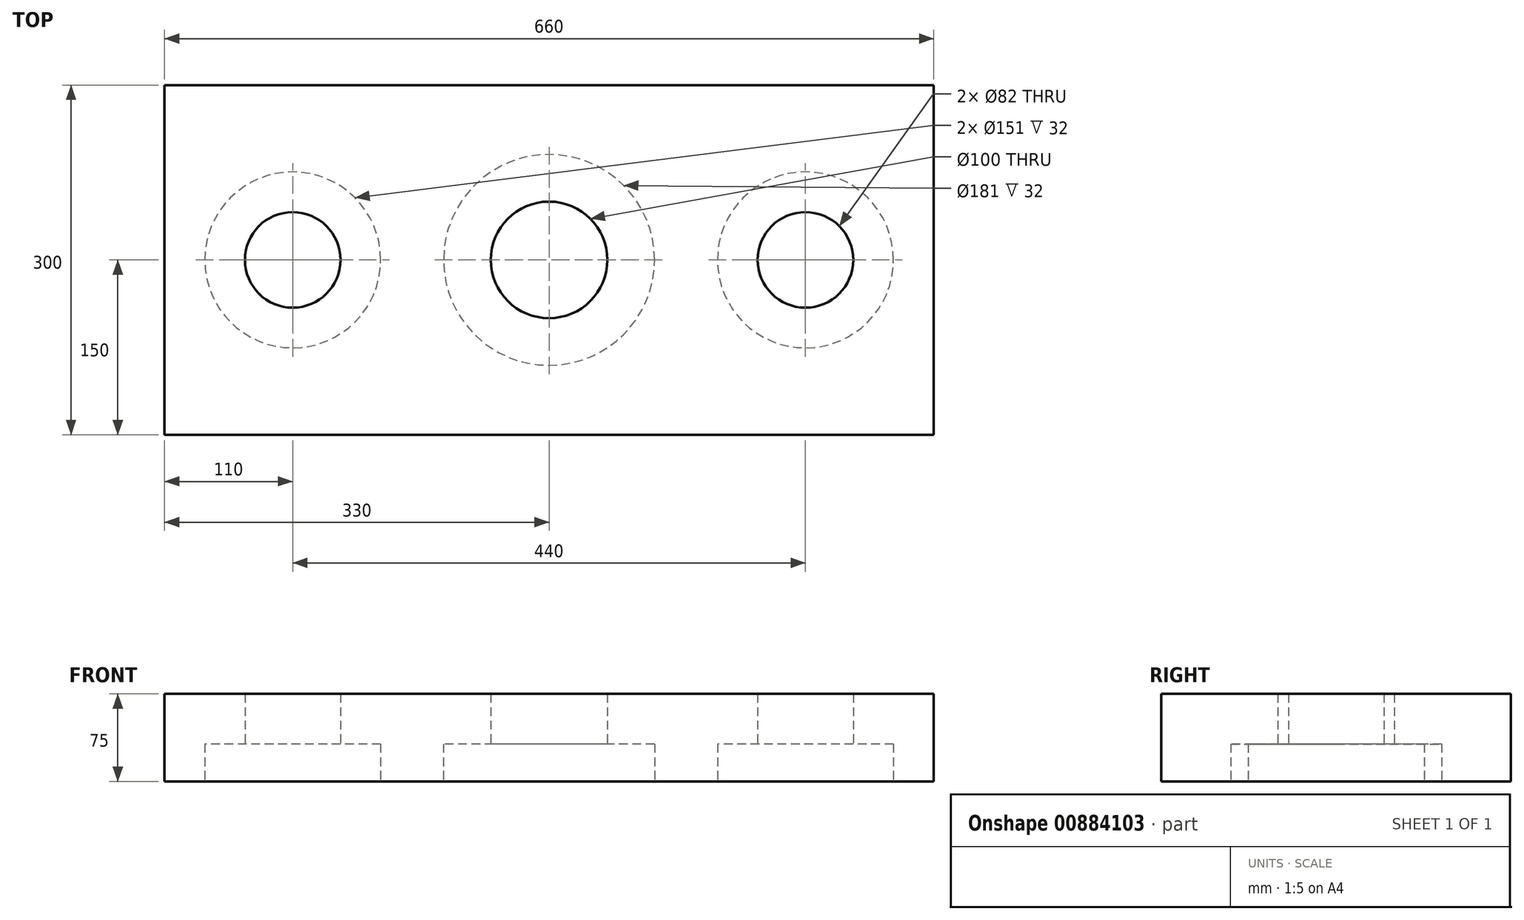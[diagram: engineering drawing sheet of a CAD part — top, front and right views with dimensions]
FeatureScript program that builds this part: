
annotation { "Feature Type Name" : "Feature", "Feature Type Description" : "" }
export const myFeature = defineFeature(function(context is Context, id is Id, definition is map)
    precondition{}
    {
        {
            var Q0;
            Q0=qCreatedBy(makeId("Top.planeOp"),FACE);
            var sketch = newSketch(context, id + "F0", { "sketchPlane" : qUnion([Q0])});
            skLineSegment(sketch, "E0.bottom", {"start": v(-330, 150) * mm, "end": v(330, 150) * mm});
            skLineSegment(sketch, "E0.top", {"start": v(-330, -150) * mm, "end": v(330, -150) * mm});
            skLineSegment(sketch, "E0.left", {"start": v(-330, 150) * mm, "end": v(-330, -150) * mm});
            skLineSegment(sketch, "E0.right", {"start": v(330, 150) * mm, "end": v(330, -150) * mm});
            skPoint(sketch, "E0.middle", {"position": v(0, 0) * mm});
            skLineSegment(sketch, "E1", {"start": v(-330, 0) * mm, "end": v(330, 0) * mm, "construction": true});
            skCircle(sketch, "E2", {"center": v(0, 0) * mm, "radius": 50 * mm});
            skCircle(sketch, "E3", {"center": v(0, 0) * mm, "radius": 90.5 * mm});
            skCircle(sketch, "E4", {"center": v(-220, 0) * mm, "radius": 41 * mm});
            skCircle(sketch, "E5", {"center": v(-220, 0) * mm, "radius": 75.5 * mm});
            skCircle(sketch, "E6", {"center": v(220, 0) * mm, "radius": 41 * mm});
            skCircle(sketch, "E7", {"center": v(220, 0) * mm, "radius": 75.5 * mm});
            skSolve(sketch);
        }
        {
            var Q0;
            Q0=makeQuery(id+"F0.imprint","IMPRINT",FACE,{"disambiguationData":[TD([[makeQuery(id+"F0.imprint","IMPRINT",EDGE,{"derivedFrom":sQuery(id+"F0.wireOp",EDGE,"E0.bottom")}),-1.0]])]});
            var Q1;
            Q1=makeQuery(id+"F0.imprint","IMPRINT",FACE,{"disambiguationData":[TD([[makeQuery(id+"F0.imprint","IMPRINT",EDGE,{"derivedFrom":sQuery(id+"F0.wireOp",EDGE,"E4")}),-1.0]])]});
            var Q2;
            Q2=makeQuery(id+"F0.imprint","IMPRINT",FACE,{"disambiguationData":[TD([[makeQuery(id+"F0.imprint","IMPRINT",EDGE,{"derivedFrom":sQuery(id+"F0.wireOp",EDGE,"E2")}),-1.0]])]});
            var Q3;
            Q3=makeQuery(id+"F0.imprint","IMPRINT",FACE,{"disambiguationData":[TD([[makeQuery(id+"F0.imprint","IMPRINT",EDGE,{"derivedFrom":sQuery(id+"F0.wireOp",EDGE,"E6")}),-1.0]])]});
            extrude(context, id + "F1", {"entities" : qUnion([Q0, Q1, Q2, Q3]), "depth" : 75 * mm, "offsetDistance" : 25 * mm});
        }
        {
            var Q0;
            Q0=makeQuery(id+"F0.imprint","IMPRINT",FACE,{"disambiguationData":[TD([[makeQuery(id+"F0.imprint","IMPRINT",EDGE,{"derivedFrom":sQuery(id+"F0.wireOp",EDGE,"E4")}),-1.0]])]});
            var Q1;
            Q1=makeQuery(id+"F0.imprint","IMPRINT",FACE,{"disambiguationData":[TD([[makeQuery(id+"F0.imprint","IMPRINT",EDGE,{"derivedFrom":sQuery(id+"F0.wireOp",EDGE,"E2")}),-1.0]])]});
            var Q2;
            Q2=makeQuery(id+"F0.imprint","IMPRINT",FACE,{"disambiguationData":[TD([[makeQuery(id+"F0.imprint","IMPRINT",EDGE,{"derivedFrom":sQuery(id+"F0.wireOp",EDGE,"E6")}),-1.0]])]});
            extrude(context, id + "F2", {"entities" : qUnion([Q0, Q1, Q2]), "operationType" : NewBodyOperationType.REMOVE, "depth" : 32 * mm, "offsetDistance" : 25 * mm});
        }
    });
